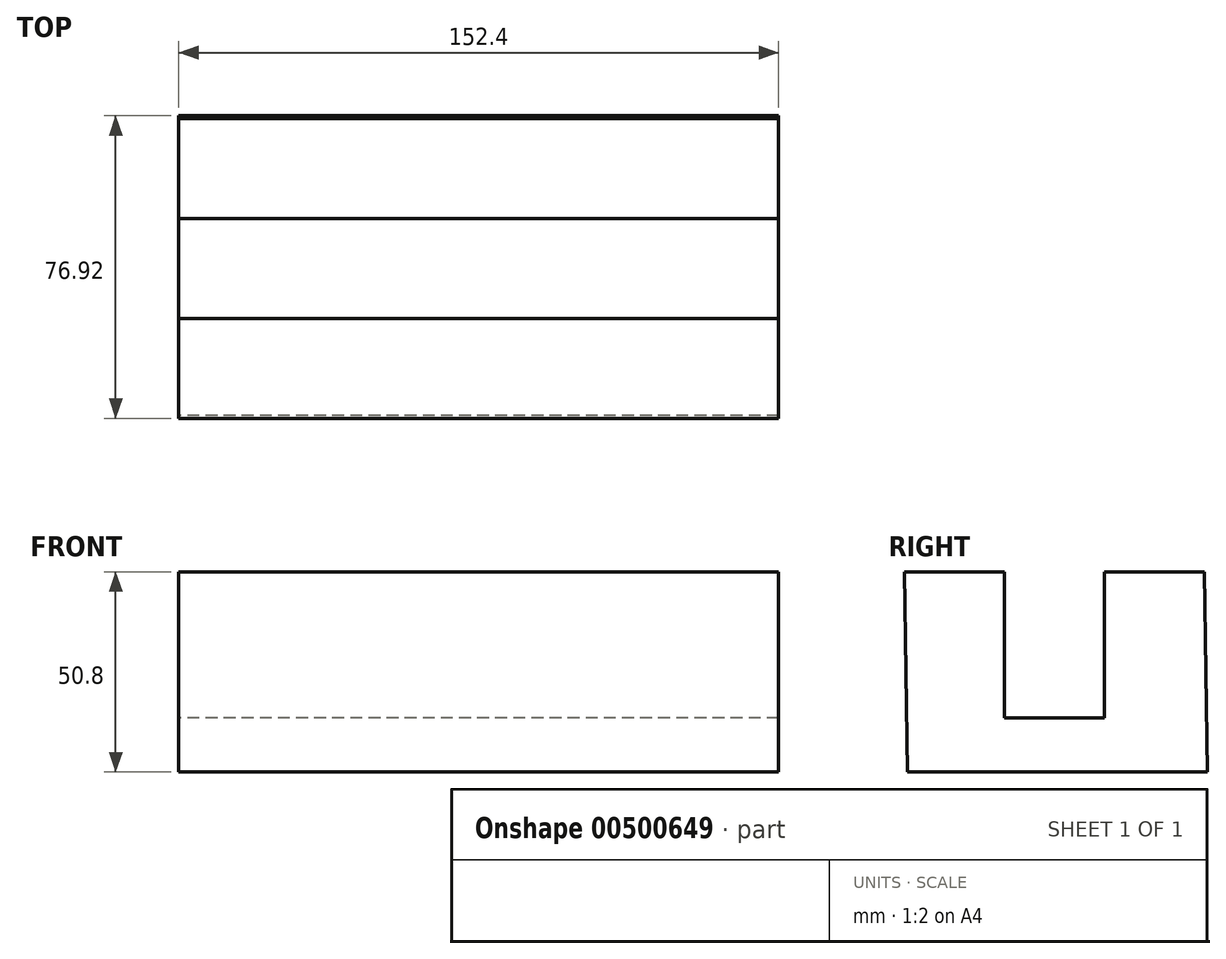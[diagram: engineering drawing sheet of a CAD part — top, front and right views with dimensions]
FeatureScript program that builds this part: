
annotation { "Feature Type Name" : "Feature", "Feature Type Description" : "" }
export const myFeature = defineFeature(function(context is Context, id is Id, definition is map)
    precondition{}
    {
        {
            var Q0;
            Q0=qCreatedBy(makeId("Right.planeOp"),FACE);
            var sketch = newSketch(context, id + "F0", { "sketchPlane" : qUnion([Q0])});
            skLineSegment(sketch, "E0", {"start": v(-28.74, 51.69) * mm, "end": v(-28.02, 0.9) * mm});
            skLineSegment(sketch, "E1", {"start": v(-28.02, 0.9) * mm, "end": v(48.18, 0.9) * mm});
            skLineSegment(sketch, "E2", {"start": v(48.18, 0.9) * mm, "end": v(47.46, 51.69) * mm});
            skLineSegment(sketch, "E3", {"start": v(47.46, 51.69) * mm, "end": v(22.06, 51.69) * mm});
            skLineSegment(sketch, "E4", {"start": v(22.06, 51.69) * mm, "end": v(22.06, 14.55) * mm});
            skLineSegment(sketch, "E5", {"start": v(-28.74, 51.69) * mm, "end": v(-3.34, 51.69) * mm});
            skLineSegment(sketch, "E6", {"start": v(-3.34, 51.69) * mm, "end": v(-3.34, 14.55) * mm});
            skLineSegment(sketch, "E7", {"start": v(-3.34, 14.55) * mm, "end": v(22.06, 14.55) * mm});
            skSolve(sketch);
        }
        {
            var Q0;
            Q0=makeQuery(id+"F0.imprint","IMPRINT",FACE,{"disambiguationData":[TD([[makeQuery(id+"F0.imprint","IMPRINT",EDGE,{"derivedFrom":sQuery(id+"F0.wireOp",EDGE,"E0")}),1.0]])]});
            extrude(context, id + "F1", {"entities" : qUnion([Q0]), "depth" : 152.4 * mm});
        }
    });
